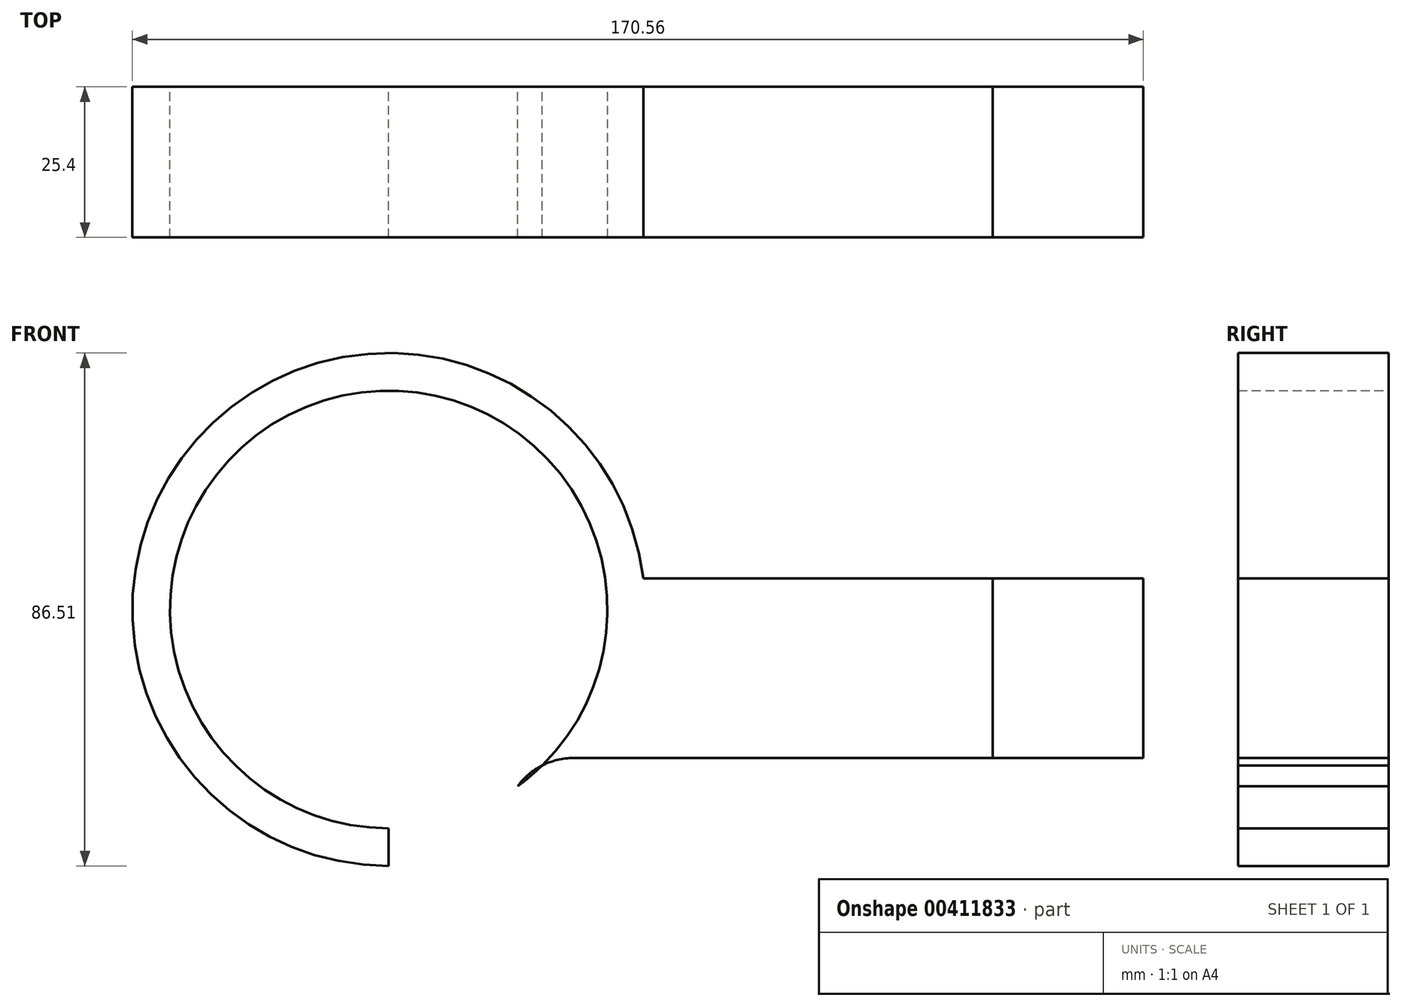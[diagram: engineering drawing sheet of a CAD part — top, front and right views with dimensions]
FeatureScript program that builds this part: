
annotation { "Feature Type Name" : "Feature", "Feature Type Description" : "" }
export const myFeature = defineFeature(function(context is Context, id is Id, definition is map)
    precondition{}
    {
        {
            var Q0;
            Q0=qCreatedBy(makeId("Front.planeOp"),FACE);
            var sketch = newSketch(context, id + "F0", { "sketchPlane" : qUnion([Q0])});
            skLineSegment(sketch, "E0.bottom", {"start": v(-41.27, -43.18) * mm, "end": v(41.28, -43.18) * mm});
            skLineSegment(sketch, "E0.top", {"start": v(-41.28, 43.18) * mm, "end": v(41.28, 43.18) * mm});
            skLineSegment(sketch, "E0.left", {"start": v(-41.27, -43.18) * mm, "end": v(-41.28, 43.18) * mm});
            skLineSegment(sketch, "E0.right", {"start": v(41.28, -43.18) * mm, "end": v(41.28, 43.18) * mm});
            skPoint(sketch, "E0.middle", {"position": v(0, 0) * mm});
            skLineSegment(sketch, "E1.bottom", {"start": v(72.43, 52.88) * mm, "end": v(143.18, 52.88) * mm});
            skLineSegment(sketch, "E1.top", {"start": v(72.43, 83.2) * mm, "end": v(143.18, 83.2) * mm});
            skLineSegment(sketch, "E1.left", {"start": v(72.43, 52.88) * mm, "end": v(72.43, 83.2) * mm});
            skLineSegment(sketch, "E1.right", {"start": v(143.18, 52.88) * mm, "end": v(143.18, 83.2) * mm});
            skPoint(sketch, "E1.middle", {"position": v(107.8, 68.04) * mm});
            skLineSegment(sketch, "E2", {"start": v(41.28, 41.03) * mm, "end": v(41.28, 43.18) * mm});
            skLineSegment(sketch, "E3", {"start": v(41.27, 41.03) * mm, "end": v(41.27, 41.03) * mm});
            skLineSegment(sketch, "E4", {"start": v(41.27, 41.03) * mm, "end": v(117.8, 41.03) * mm});
            skArc(sketch, "E5", {"start": v(72.43, 52.88) * mm, "mid": v(67.15, 51.62) * mm, "end": v(63.01, 48.11) * mm});
            skArc(sketch, "E6", {"start": v(41.27, 41.03) * mm, "mid": v(29.85, 113.02) * mm, "end": v(63.01, 48.11) * mm});
            skArc(sketch, "E7.0", {"start": v(41.27, 34.68) * mm, "mid": v(27.27, 118.86) * mm, "end": v(67.77, 43.75) * mm});
            skFitSpline(sketch, "E8", {"points": [v(-41.28, 43.18) * mm, v(6.18, 103.22) * mm, v(72.43, 83.2) * mm], "startDerivative": vector(17.95, 186.29) * mm, "endDerivative": vector(140.33, -62.7) * mm});
            skSolve(sketch);
        }
        {
            var Q0;
            {var subQ0=sQuery(id+"F0.wireOp",EDGE,"E6");var subQ1=sQuery(id+"F0.wireOp",EDGE,"E5");var subQ2=makeQuery(id+"F0.imprint","INTERSECT",VERTEX,{"disambiguationData":[OD(0.0)],"derivedFrom":[subQ1,subQ0]});Q0=makeQuery(id+"F0.imprint","IMPRINT",FACE,{"disambiguationData":[TD([[makeQuery(id+"F0.imprint","IMPRINT",EDGE,{"disambiguationData":[TD([[subQ2,1.0]])],"derivedFrom":subQ1}),1.0]])]});}
            var Q1;
            {var subQ0=sQuery(id+"F0.wireOp",EDGE,"E2");Q1=makeQuery(id+"F0.imprint","IMPRINT",FACE,{"disambiguationData":[TD([[makeQuery(id+"F0.imprint","IMPRINT",EDGE,{"derivedFrom":subQ0}),1.0]])]});}
            var Q2;
            {var subQ0=sQuery(id+"F0.wireOp",EDGE,"E1.right");Q2=makeQuery(id+"F0.imprint","IMPRINT",FACE,{"disambiguationData":[TD([[makeQuery(id+"F0.imprint","IMPRINT",EDGE,{"derivedFrom":subQ0}),1.0]])]});}
            var Q3;
            {var subQ0=sQuery(id+"F0.wireOp",EDGE,"E5");var subQ3=sQuery(id+"F0.wireOp",EDGE,"E6");var subQ5=makeQuery(id+"F0.imprint","INTERSECT",VERTEX,{"disambiguationData":[OD(1.0)],"derivedFrom":[subQ0,subQ3]});Q3=makeQuery(id+"F0.imprint","IMPRINT",FACE,{"disambiguationData":[TD([[makeQuery(id+"F0.imprint","IMPRINT",EDGE,{"disambiguationData":[TD([[subQ5,1.0]])],"derivedFrom":subQ3}),1.0]])]});}
            var Q4;
            {var subQ0=sQuery(id+"F0.wireOp",EDGE,"E8");var subQ3=sQuery(id+"F0.wireOp",EDGE,"E7.0");var subQ5=makeQuery(id+"F0.imprint","INTERSECT",VERTEX,{"derivedFrom":[subQ3,subQ0]});Q4=makeQuery(id+"F0.imprint","IMPRINT",FACE,{"disambiguationData":[TD([[makeQuery(id+"F0.imprint","IMPRINT",EDGE,{"disambiguationData":[TD([[subQ5,1.0]])],"derivedFrom":subQ3}),1.0]])]});}
            var Q5;
            {var subQ0=sQuery(id+"F0.wireOp",EDGE,"E1.left");var subQ3=sQuery(id+"F0.wireOp",EDGE,"E6");var subQ5=makeQuery(id+"F0.imprint","INTERSECT",VERTEX,{"derivedFrom":[subQ0,subQ3]});Q5=makeQuery(id+"F0.imprint","IMPRINT",FACE,{"disambiguationData":[TD([[makeQuery(id+"F0.imprint","IMPRINT",EDGE,{"disambiguationData":[TD([[subQ5,1.0]])],"derivedFrom":subQ3}),-1.0]])]});}
            var Q6;
            {var subQ0=sQuery(id+"F0.wireOp",EDGE,"E8");var subQ3=sQuery(id+"F0.wireOp",EDGE,"E6");var subQ5=makeQuery(id+"F0.imprint","INTERSECT",VERTEX,{"derivedFrom":[subQ3,subQ0]});Q6=makeQuery(id+"F0.imprint","IMPRINT",FACE,{"disambiguationData":[TD([[makeQuery(id+"F0.imprint","IMPRINT",EDGE,{"disambiguationData":[TD([[subQ5,-1.0]])],"derivedFrom":subQ3}),-1.0]])]});}
            var Q7;
            {var subQ0=sQuery(id+"F0.wireOp",EDGE,"E6");var subQ1=sQuery(id+"F0.wireOp",EDGE,"E0.top");var subQ2=makeQuery(id+"F0.imprint","INTERSECT",VERTEX,{"derivedFrom":[subQ1,subQ0]});Q7=makeQuery(id+"F0.imprint","IMPRINT",FACE,{"disambiguationData":[TD([[makeQuery(id+"F0.imprint","IMPRINT",EDGE,{"disambiguationData":[TD([[subQ2,1.0]])],"derivedFrom":subQ1}),-1.0]])]});}
            var Q8;
            {var subQ0=sQuery(id+"F0.wireOp",EDGE,"E6");var subQ1=sQuery(id+"F0.wireOp",EDGE,"E0.top");var subQ2=makeQuery(id+"F0.imprint","INTERSECT",VERTEX,{"derivedFrom":[subQ1,subQ0]});Q8=makeQuery(id+"F0.imprint","IMPRINT",FACE,{"disambiguationData":[TD([[makeQuery(id+"F0.imprint","IMPRINT",EDGE,{"disambiguationData":[TD([[subQ2,1.0]])],"derivedFrom":subQ1}),1.0]])]});}
            var Q9;
            {var subQ0=sQuery(id+"F0.wireOp",EDGE,"E7.0");var subQ1=sQuery(id+"F0.wireOp",EDGE,"E1.top");var subQ2=makeQuery(id+"F0.imprint","INTERSECT",VERTEX,{"derivedFrom":[subQ1,subQ0]});Q9=makeQuery(id+"F0.imprint","IMPRINT",FACE,{"disambiguationData":[TD([[makeQuery(id+"F0.imprint","IMPRINT",EDGE,{"disambiguationData":[TD([[subQ2,1.0]])],"derivedFrom":subQ1}),1.0]])]});}
            var Q10;
            {var subQ3=sQuery(id+"F0.wireOp",EDGE,"E1.top");var subQ5=sQuery(id+"F0.wireOp",EDGE,"E7.0");var subQ6=makeQuery(id+"F0.imprint","INTERSECT",VERTEX,{"derivedFrom":[subQ3,subQ5]});Q10=makeQuery(id+"F0.imprint","IMPRINT",FACE,{"disambiguationData":[TD([[makeQuery(id+"F0.imprint","IMPRINT",EDGE,{"disambiguationData":[TD([[subQ6,1.0]])],"derivedFrom":subQ3}),-1.0]])]});}
            extrude(context, id + "F1", {"entities" : qUnion([Q0, Q1, Q2, Q3, Q4, Q5, Q6, Q7, Q8, Q9, Q10]), "depth" : 25.4 * mm});
        }
        {
            var Q0;
            Q0=makeQuery(id+"F1.opExtrude","SWEPT_FACE",FACE,{"disambiguationData":[OSD([sQuery(id+"F0.wireOp",EDGE,"E1.right")])]});
            extrude(context, id + "F2", {"entities" : qUnion([Q0]), "depth" : 25.4 * mm});
        }
    });
